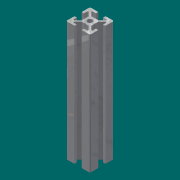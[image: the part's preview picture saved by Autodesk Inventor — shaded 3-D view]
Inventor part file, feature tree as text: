
AUTODESK INVENTOR PART (.ipt)
format: ipt  version: 2016 SP1 (Build 200210100, 210)  size: 154,624 bytes
history: native  units: mm
features: extrude x1, sketch x1
ambient origin geometry x8: Origin, YZ Plane, XZ Plane, XY Plane, X Axis, Y Axis, Z Axis, Center Point
bodies: Solid1 (feature_tree)
feature tree (2):
  extrude  "Extrusion1"  [1 undecoded]
  sketch  "Sketch1"  dims[d0=100.0mm d1=0.0mm]
note: 1 required parameter value undecoded (feature->parameter linkage not recoverable at this tier; creation-order binding heuristic only, values carry confidence <= 0.55)
